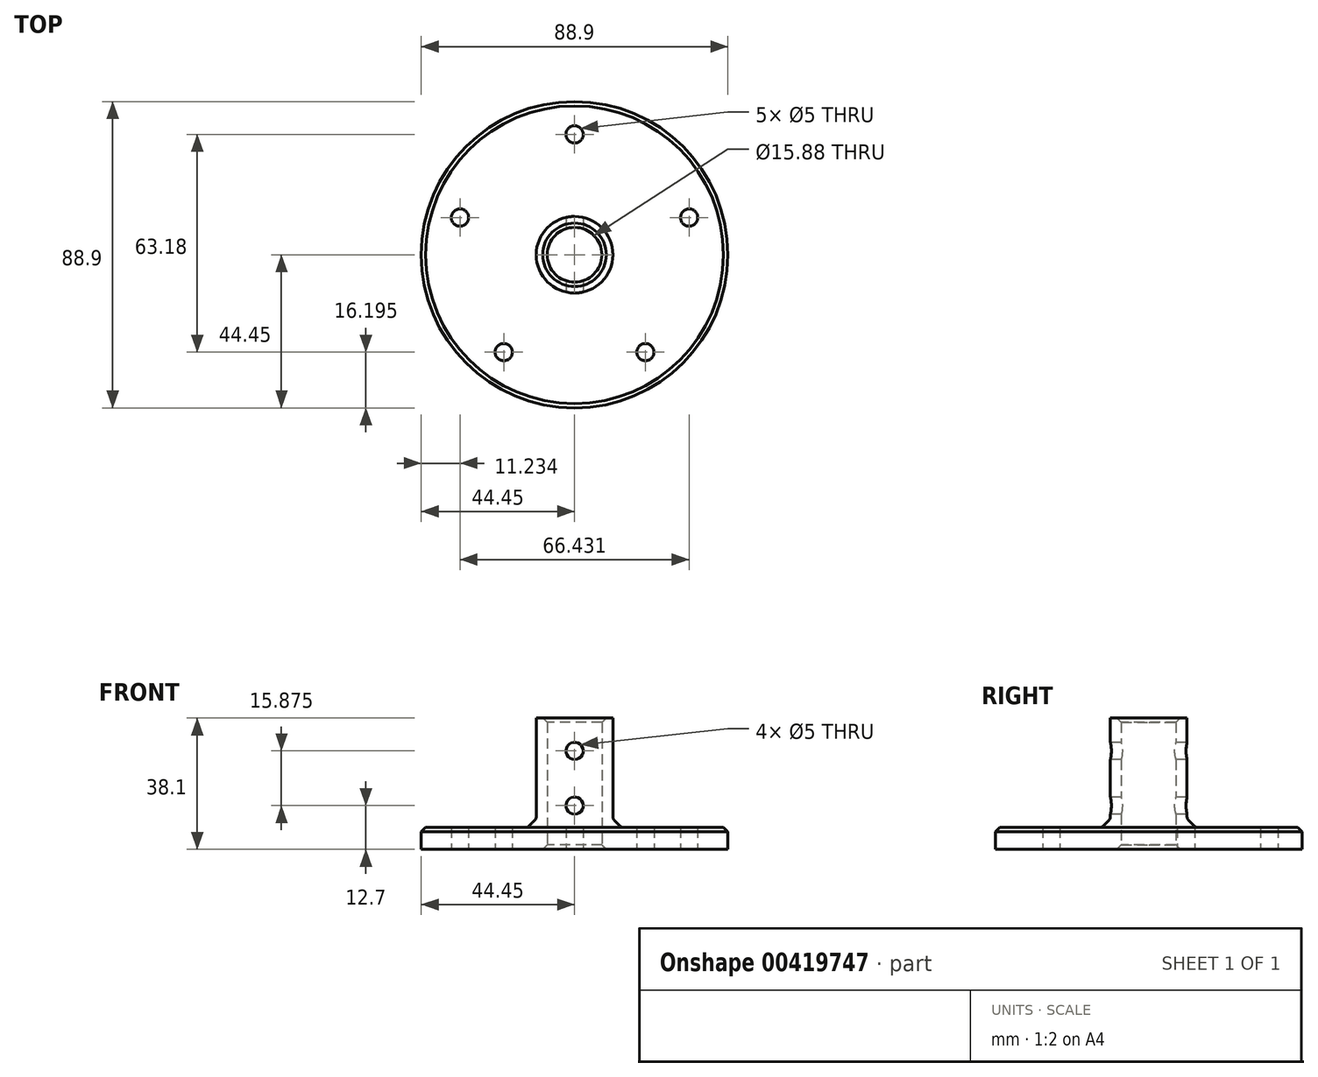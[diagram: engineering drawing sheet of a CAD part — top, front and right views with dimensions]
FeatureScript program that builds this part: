
annotation { "Feature Type Name" : "Feature", "Feature Type Description" : "" }
export const myFeature = defineFeature(function(context is Context, id is Id, definition is map)
    precondition{}
    {
        {
            var Q0;
            Q0=qCreatedBy(makeId("Top.planeOp"),FACE);
            var sketch = newSketch(context, id + "F0", { "sketchPlane" : qUnion([Q0])});
            skCircle(sketch, "E0", {"center": v(0, 0) * mm, "radius": 44.45 * mm});
            skCircle(sketch, "E1", {"center": v(0, 34.93) * mm, "radius": 2.5 * mm});
            skCircle(sketch, "E2", {"center": v(0, 0) * mm, "radius": 7.94 * mm});
            skCircle(sketch, "E3", {"center": v(0, 0) * mm, "radius": 11.11 * mm});
            skCircle(sketch, "E4.1.0", {"center": v(-33.22, 10.8) * mm, "radius": 2.5 * mm});
            skCircle(sketch, "E4.2.0", {"center": v(-20.53, -28.25) * mm, "radius": 2.5 * mm});
            skCircle(sketch, "E4.3.0", {"center": v(20.53, -28.25) * mm, "radius": 2.5 * mm});
            skCircle(sketch, "E4.4.0", {"center": v(33.22, 10.8) * mm, "radius": 2.5 * mm});
            skSolve(sketch);
        }
        {
            var Q0;
            Q0=makeQuery(id+"F0.imprint","IMPRINT",FACE,{"disambiguationData":[TD([[makeQuery(id+"F0.imprint","IMPRINT",EDGE,{"derivedFrom":sQuery(id+"F0.wireOp",EDGE,"E0")}),1.0]])]});
            var Q1;
            Q1=makeQuery(id+"F0.imprint","IMPRINT",FACE,{"disambiguationData":[TD([[makeQuery(id+"F0.imprint","IMPRINT",EDGE,{"derivedFrom":sQuery(id+"F0.wireOp",EDGE,"E2")}),-1.0]])]});
            extrude(context, id + "F1", {"entities" : qUnion([Q0, Q1]), "depth" : 6.35 * mm});
        }
        {
            var Q0;
            Q0=makeQuery(id+"F0.imprint","IMPRINT",FACE,{"disambiguationData":[TD([[makeQuery(id+"F0.imprint","IMPRINT",EDGE,{"derivedFrom":sQuery(id+"F0.wireOp",EDGE,"E2")}),-1.0]])]});
            extrude(context, id + "F2", {"entities" : qUnion([Q0]), "operationType" : NewBodyOperationType.ADD, "depth" : 38.1 * mm});
        }
        {
            var Q0;
            Q0=qCreatedBy(makeId("Front.planeOp"),FACE);
            var sketch = newSketch(context, id + "F3", { "sketchPlane" : qUnion([Q0])});
            skCircle(sketch, "E5", {"center": v(0, 12.7) * mm, "radius": 2.5 * mm});
            skCircle(sketch, "E6", {"center": v(0, 28.58) * mm, "radius": 2.5 * mm});
            skSolve(sketch);
        }
        {
            var Q0;
            Q0 = qSketchRegion(id + "F3", true);
            extrude(context, id + "F4", {"entities" : qUnion([Q0]), "operationType" : NewBodyOperationType.REMOVE, "endBound" : BoundingType.THROUGH_ALL, "oppositeDirection" : true, "depth" : 25.4 * mm, "hasSecondDirection" : true, "secondDirectionBound" : SecondDirectionBoundingType.THROUGH_ALL, "secondDirectionOppositeDirection" : false, "secondDirectionDepth" : 25.4 * mm});
        }
        {
            var Q0;
            Q0=makeQuery(id+"F2.opExtrude","CAP_EDGE",EDGE,{"disambiguationData":[OSD([sQuery(id+"F0.wireOp",EDGE,"E2")])],"isStart":false});
            var Q1;
            Q1=makeQuery(id+"F1.opExtrude","CAP_EDGE",EDGE,{"disambiguationData":[OSD([sQuery(id+"F0.wireOp",EDGE,"E2")])],"isStart":true});
            var Q2;
            Q2=makeQuery(id+"F1.opExtrude","CAP_EDGE",EDGE,{"disambiguationData":[OSD([sQuery(id+"F0.wireOp",EDGE,"E0")])],"isStart":false});
            chamfer(context, id + "F5", {"entities" : qUnion([Q0, Q1, Q2]), "width" : 1.27 * mm, "tangentPropagation" : true});
        }
        {
            var Q0;
            Q0=makeQuery(id+"F2.boolean.opBoolean","INTERSECT",EDGE,{"derivedFrom":[makeQuery(id+"F1.opExtrude","CAP_FACE",FACE,{"disambiguationData":[OSD([sQuery(id+"F0.wireOp",EDGE,"E0"),sQuery(id+"F0.wireOp",EDGE,"E1"),sQuery(id+"F0.wireOp",EDGE,"E2"),sQuery(id+"F0.wireOp",EDGE,"E4.1.0"),sQuery(id+"F0.wireOp",EDGE,"E4.2.0"),sQuery(id+"F0.wireOp",EDGE,"E4.3.0"),sQuery(id+"F0.wireOp",EDGE,"E4.4.0")])],"isStart":false}),makeQuery(id+"F2.opExtrude","SWEPT_FACE",FACE,{"disambiguationData":[OSD([sQuery(id+"F0.wireOp",EDGE,"E3")])]})]});
            chamfer(context, id + "F6", {"entities" : qUnion([Q0]), "width" : 2.54 * mm, "tangentPropagation" : true});
        }
        {
            var Q0;
            {var subQ0=makeQuery(id+"F2.opExtrude","SWEPT_FACE",FACE,{"disambiguationData":[OSD([sQuery(id+"F0.wireOp",EDGE,"E3")])]});Q0=makeQuery(id+"F6.opChamfer","BLEND_EDGE",EDGE,{"blendedFrom":[makeQuery(id+"F2.boolean.opBoolean","INTERSECT",EDGE,{"derivedFrom":[makeQuery(id+"F1.opExtrude","CAP_FACE",FACE,{"disambiguationData":[OSD([sQuery(id+"F0.wireOp",EDGE,"E0"),sQuery(id+"F0.wireOp",EDGE,"E1"),sQuery(id+"F0.wireOp",EDGE,"E2"),sQuery(id+"F0.wireOp",EDGE,"E4.1.0"),sQuery(id+"F0.wireOp",EDGE,"E4.2.0"),sQuery(id+"F0.wireOp",EDGE,"E4.3.0"),sQuery(id+"F0.wireOp",EDGE,"E4.4.0")])],"isStart":false}),subQ0]}),subQ0],"blendedInto":[subQ0]});}
            var Q1;
            {var subQ0=makeQuery(id+"F1.opExtrude","CAP_FACE",FACE,{"disambiguationData":[OSD([sQuery(id+"F0.wireOp",EDGE,"E0"),sQuery(id+"F0.wireOp",EDGE,"E1"),sQuery(id+"F0.wireOp",EDGE,"E2"),sQuery(id+"F0.wireOp",EDGE,"E4.1.0"),sQuery(id+"F0.wireOp",EDGE,"E4.2.0"),sQuery(id+"F0.wireOp",EDGE,"E4.3.0"),sQuery(id+"F0.wireOp",EDGE,"E4.4.0")])],"isStart":false});Q1=makeQuery(id+"F6.opChamfer","BLEND_EDGE",EDGE,{"blendedFrom":[makeQuery(id+"F2.boolean.opBoolean","INTERSECT",EDGE,{"derivedFrom":[subQ0,makeQuery(id+"F2.opExtrude","SWEPT_FACE",FACE,{"disambiguationData":[OSD([sQuery(id+"F0.wireOp",EDGE,"E3")])]})]}),subQ0],"blendedInto":[subQ0]});}
            fillet(context, id + "F7", {"entities" : qUnion([Q0, Q1]), "radius" : 1.52 * mm, "tangentPropagation" : true, "allowEdgeOverflow" : false});
        }
    });
